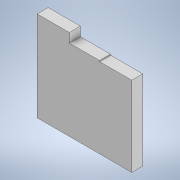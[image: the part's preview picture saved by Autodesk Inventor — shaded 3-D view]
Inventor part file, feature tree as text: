
AUTODESK INVENTOR PART (.ipt)
format: ipt  version: 2020.1 (Build 241239000, 239)  size: 105,984 bytes
history: native  units: in
note: dims shown in document units (in); Inventor stores cm internally (conversion verified against a paired STEP export)
features: extrude x1, sketch x1
ambient origin geometry x8: Origin, YZ Plane, XZ Plane, XY Plane, X Axis, Y Axis, Z Axis, Center Point
bodies: Solid1 (feature_tree)
feature tree (2):
  extrude  "Extrusion1"  Depth=98.0in
  sketch  "Sketch1"  dims[d0=35.0in d1=98.0in d2=33.0in d3=88.0in d4=35.0in d5=87.0in d6=33.0in d7=98.0in d8=12.0in d9=0.0in d10=136.0in]
